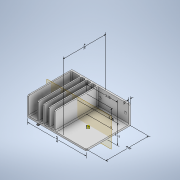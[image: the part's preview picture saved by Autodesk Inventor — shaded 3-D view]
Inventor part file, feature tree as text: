
AUTODESK INVENTOR PART (.ipt)
format: ipt  version: 2021.2 (Build 252289000, 289)  size: 369,664 bytes
history: native  units: in
note: dims shown in document units (in); Inventor stores cm internally (conversion verified against a paired STEP export)
features: other x8, fillet x6, sketch x6, extrude x5, hole x1, mirror x1
ambient origin geometry x8: Origin, YZ Plane, XZ Plane, XY Plane, X Axis, Y Axis, Z Axis, Center Point
bodies: Solid1 (feature_tree)
feature tree (27):
  other  "Annotations"
  extrude  "Extrusion1"  Depth=6.625in
  extrude  "Extrusion7"  Depth=0.1875in
  extrude  "Extrusion8"  TaperAngle=0.0deg  [1 undecoded]
  hole  "Hole2"  [1 undecoded]
  fillet  "Fillet1"  Radius=0.125in
  fillet  "Fillet2"  Radius=0.125in
  fillet  "Fillet3"  Radius=1.0in
  extrude  "Extrusion10"  Depth=0.5in
  extrude  "Extrusion11"  Depth=0.1875in
  fillet  "Fillet4"  Radius=2.0in
  fillet  "Fillet5"  [1 undecoded]
  fillet  "Fillet6"  Radius=1.0in
  mirror  "Mirror4"
  sketch  "Sketch2"  dims[d0=5.0in d1=6.625in]
  sketch  "Sketch11"  dims[d2=0.1875in d3=0.0in d52=0.1875in]
  sketch  "Sketch12"  dims[d53=2.0in d54=0.0in]
  sketch  "Sketch13"  dims[d55=0.125in d56=0.125in d57=0.125in d58=0.125in d59=1.0in]
  sketch  "Sketch15"  dims[d60=0.5in d61=0.5in]
  sketch  "Sketch16"  dims[d62=0.125in d63=0.5in d64=2.0in d65=0.0in d71=1.0in d72=0.375in d73=0.375in d74=3.25in d75=0.15in d76=0.75in d77=0.279in d78=0.25in d79=0.5635in d80=1.0in d81=0.8108in d82=0.125in d83=0.125in d84=0.125in d99=0.25in d101=0.75in d102=0.5in d103=0.75in d104=0.0in d105=0.5in d106=0.5in d108=0.0in d109=0.0in d110=0.5in d111=0.125in d112=0.0625in d113=0.0625in d114=0.0625in d115=0.09in d116=0.3369in d117=4.8125in d66=0.2978in d67=0.1958in d68=3.5in d69=0.2862in d70=4.8125in d85=0.3706in d86=0.1875in d87=0.1043in d88=0.2986in d89=2.0in d94=0.0737in d95=6.625in d96=0.182in d97=0.2583in d98=2.1875in]
  other  "Linear Dimension 8"
  other  "Linear Dimension 9"
  other  "Linear Dimension 10"
  other  "Linear Dimension 11"
  other  "Linear Dimension 12"
  other  "Linear Dimension 13"
  other  "Linear Dimension 14"
note: 3 required parameter values undecoded (feature->parameter linkage not recoverable at this tier; creation-order binding heuristic only, values carry confidence <= 0.55)
